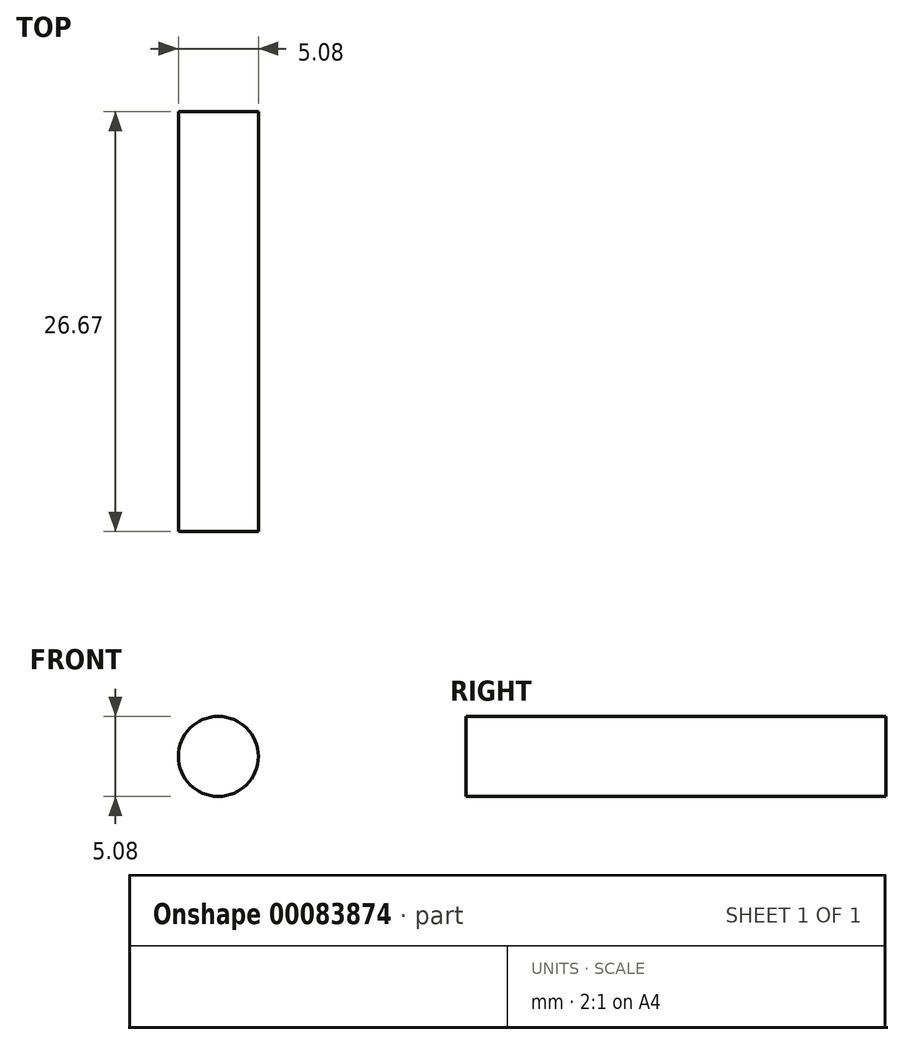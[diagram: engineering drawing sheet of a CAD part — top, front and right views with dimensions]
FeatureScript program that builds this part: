
annotation { "Feature Type Name" : "Feature", "Feature Type Description" : "" }
export const myFeature = defineFeature(function(context is Context, id is Id, definition is map)
    precondition{}
    {
        {
            var Q0;
            Q0=qCreatedBy(makeId("Front.planeOp"),FACE);
            var sketch = newSketch(context, id + "F0", { "sketchPlane" : qUnion([Q0])});
            skCircle(sketch, "E0", {"center": v(0, 0) * mm, "radius": 2.54 * mm});
            skSolve(sketch);
        }
        {
            var Q0;
            Q0=makeQuery(id+"F0.imprint","IMPRINT",FACE,{"disambiguationData":[TD([[makeQuery(id+"F0.imprint","IMPRINT",EDGE,{"derivedFrom":sQuery(id+"F0.wireOp",EDGE,"E0")}),1.0]])]});
            extrude(context, id + "F1", {"entities" : qUnion([Q0]), "depth" : 26.67 * mm});
        }
    });
